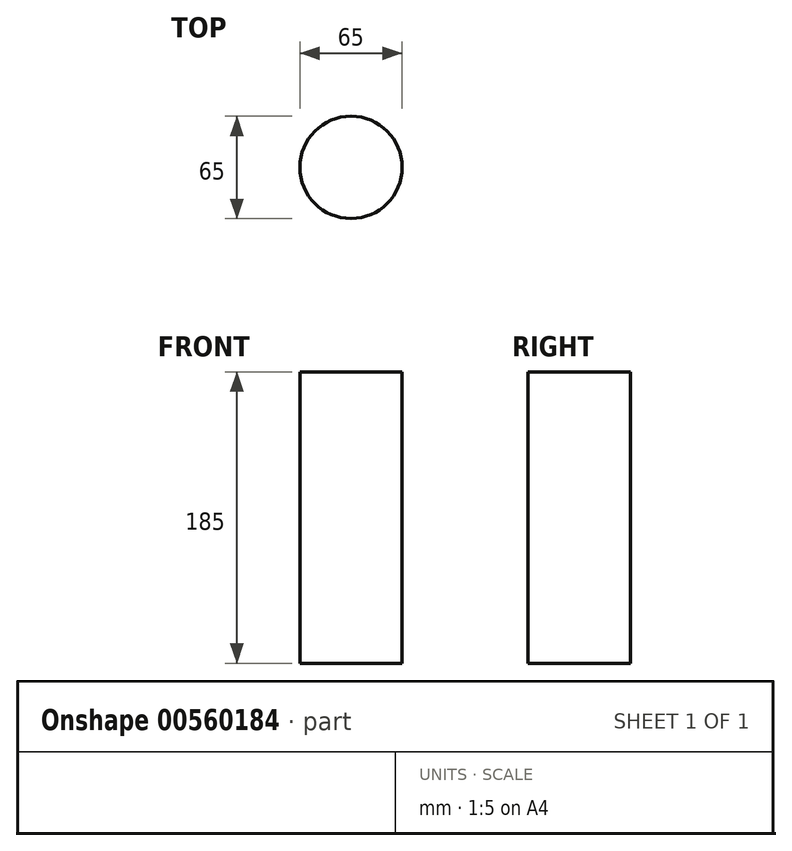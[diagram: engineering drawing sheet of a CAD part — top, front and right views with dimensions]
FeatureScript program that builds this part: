
annotation { "Feature Type Name" : "Feature", "Feature Type Description" : "" }
export const myFeature = defineFeature(function(context is Context, id is Id, definition is map)
    precondition{}
    {
        {
            var Q0;
            Q0=qCreatedBy(makeId("Top.planeOp"),FACE);
            var sketch = newSketch(context, id + "F0", { "sketchPlane" : qUnion([Q0])});
            skCircle(sketch, "E0", {"center": v(0, 0) * mm, "radius": 32.5 * mm});
            skSolve(sketch);
        }
        {
            var Q0;
            Q0 = qSketchRegion(id + "F0", true);
            extrude(context, id + "F1", {"entities" : qUnion([Q0]), "oppositeDirection" : true, "depth" : 185 * mm, "offsetDistance" : 25 * mm});
        }
    });
